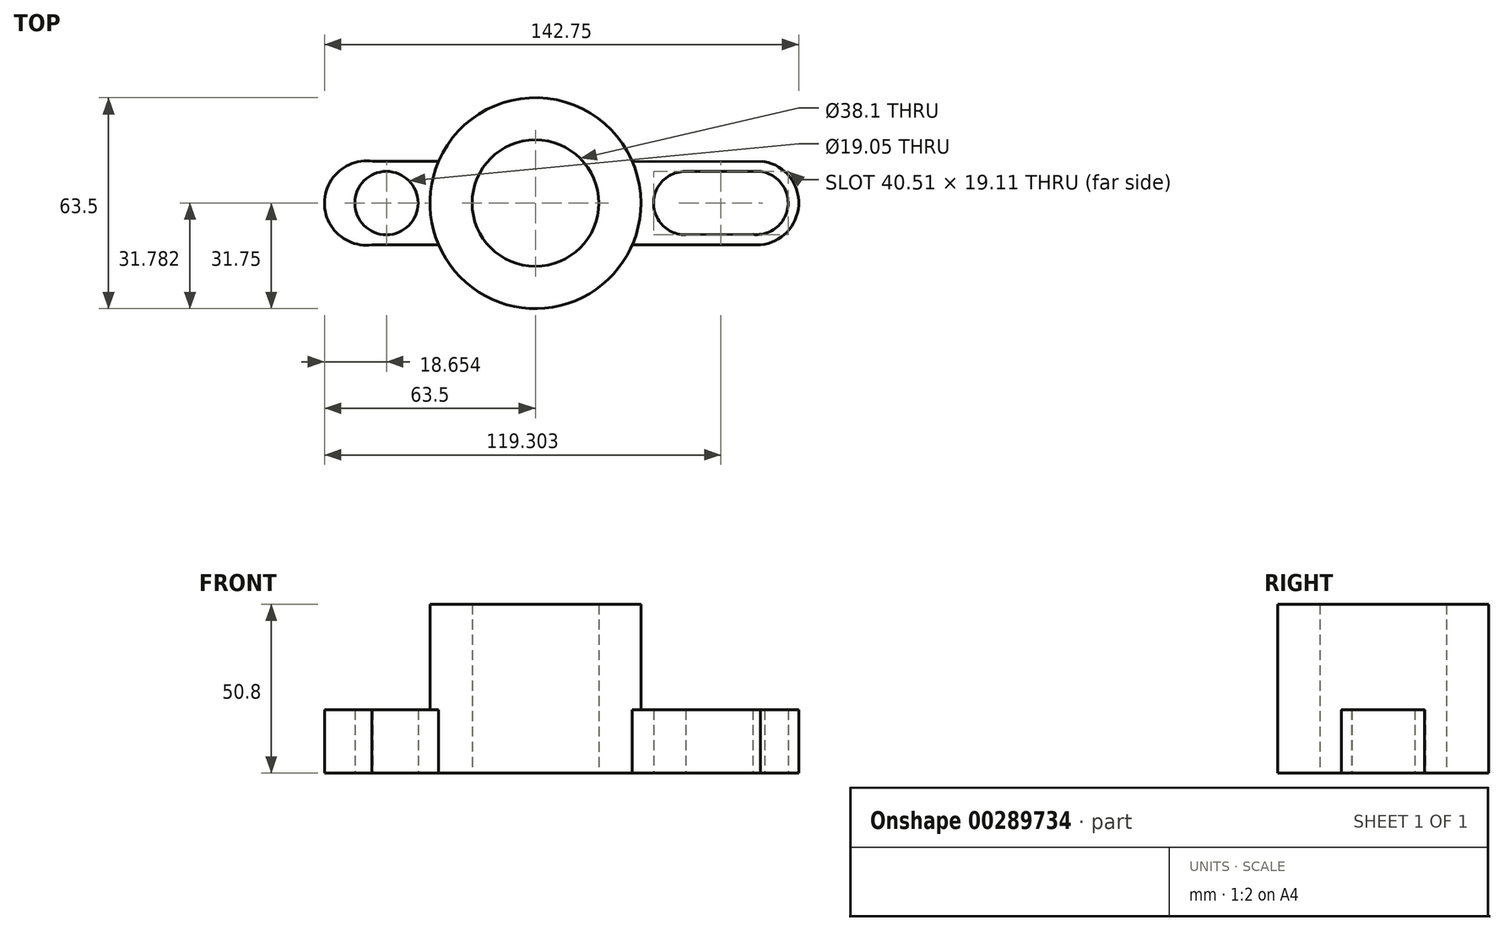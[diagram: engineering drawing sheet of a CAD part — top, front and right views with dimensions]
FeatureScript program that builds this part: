
annotation { "Feature Type Name" : "Feature", "Feature Type Description" : "" }
export const myFeature = defineFeature(function(context is Context, id is Id, definition is map)
    precondition{}
    {
        {
            var Q0;
            Q0=qCreatedBy(makeId("Top.planeOp"),FACE);
            var sketch = newSketch(context, id + "F0", { "sketchPlane" : qUnion([Q0])});
            skCircle(sketch, "E0", {"center": v(0, 0) * mm, "radius": 31.75 * mm});
            skCircle(sketch, "E1", {"center": v(0, 0) * mm, "radius": 19.05 * mm});
            skCircle(sketch, "E2", {"center": v(0, 0) * mm, "radius": 12.7 * mm});
            skArc(sketch, "E3", {"start": v(-48.95, 12.56) * mm, "mid": v(-63.5, 0.13) * mm, "end": v(-49.2, -12.6) * mm});
            skArc(sketch, "E4", {"start": v(67.72, -12.58) * mm, "mid": v(79.23, -0.58) * mm, "end": v(68.99, 12.53) * mm});
            skLineSegment(sketch, "E5", {"start": v(-48.95, 12.56) * mm, "end": v(-29.16, 12.56) * mm});
            skLineSegment(sketch, "E6", {"start": v(-49.2, -12.6) * mm, "end": v(-29.14, -12.6) * mm});
            skPoint(sketch, "E7.center.orphan", {"position": v(-44.85, 0) * mm});
            skArc(sketch, "E8", {"start": v(38.9, 5.84) * mm, "mid": v(38.7, 5.85) * mm, "end": v(38.48, 5.84) * mm});
            skLineSegment(sketch, "E9.trimOffspring", {"start": v(29.17, 12.54) * mm, "end": v(68.99, 12.53) * mm});
            skLineSegment(sketch, "E10.trimOffspring", {"start": v(29.15, -12.59) * mm, "end": v(67.72, -12.58) * mm});
            skCircle(sketch, "E11", {"center": v(-44.85, 0) * mm, "radius": 9.53 * mm});
            skPoint(sketch, "E12.center.orphan", {"position": v(66.55, 0) * mm});
            skPoint(sketch, "E12.start.orphan", {"position": v(66.55, -5.44) * mm});
            skArc(sketch, "E13", {"start": v(65.49, -9.4) * mm, "mid": v(76.06, -0.45) * mm, "end": v(66.52, 9.59) * mm});
            skArc(sketch, "E14", {"start": v(45.09, 9.52) * mm, "mid": v(35.55, -0.08) * mm, "end": v(45.25, -9.52) * mm});
            skLineSegment(sketch, "E15", {"start": v(45.09, 9.52) * mm, "end": v(66.52, 9.59) * mm});
            skLineSegment(sketch, "E16", {"start": v(45.25, -9.52) * mm, "end": v(67.72, -9.4) * mm});
            skSolve(sketch);
        }
        {
            var Q0;
            Q0=makeQuery(id+"F0.imprint","IMPRINT",FACE,{"disambiguationData":[TD([[makeQuery(id+"F0.imprint","IMPRINT",EDGE,{"derivedFrom":sQuery(id+"F0.wireOp",EDGE,"E1")}),-1.0]])]});
            extrude(context, id + "F1", {"entities" : qUnion([Q0]), "flatOperationType" : FlatOperationType.REMOVE, "offsetDistance" : 25.4 * mm, "depth" : 50.8 * mm, "domain" : OperationDomain.MODEL});
        }
        {
            var Q0;
            Q0=makeQuery(id+"F0.imprint","IMPRINT",FACE,{"disambiguationData":[TD([[makeQuery(id+"F0.imprint","IMPRINT",EDGE,{"derivedFrom":sQuery(id+"F0.wireOp",EDGE,"E3")}),1.0]])]});
            extrude(context, id + "F2", {"entities" : qUnion([Q0]), "operationType" : NewBodyOperationType.ADD, "depth" : 19.05 * mm});
        }
        {
            var Q0;
            Q0=makeQuery(id+"F0.imprint","IMPRINT",FACE,{"disambiguationData":[TD([[makeQuery(id+"F0.imprint","IMPRINT",EDGE,{"derivedFrom":sQuery(id+"F0.wireOp",EDGE,"E4")}),1.0]])]});
            extrude(context, id + "F3", {"entities" : qUnion([Q0]), "operationType" : NewBodyOperationType.ADD, "depth" : 19.05 * mm});
        }
    });
